# Revit family: Faucet-Lavatory-Grohe-Grandera-23312_Series
name_source: partatom
category: Plumbing Fixtures
revit_build: Autodesk Revit 2014 (Build: 20130308_1515(x64)
units: mm (PartAtom-declared; Revit-internal decimal feet)

## types (4) — shared parameters
ADA Compliant = Yes
Assembly Code = D2020300
CW Connection = Yes
CWFU = 1.5
CalGreen Compliant = Yes
Cold Water Connection Diameter = 3/8"
Default Elevation = 0"
Description = Grandera Single-lever basin mixer 1/2" M-Size
HW Connection = Yes
HWFU = 1.5
Height = 6 7/8"
Hot Water Connection Diameter = 0"
Installation Type = Deck-Mounted
Length = 4 3/8"
Manufacturer = Grohe
Price = Prices may vary. Please consult Manufacturer Representative for most up-to-date price list.
Product Page URL = https://www.grohe.com
URL = http://www.grohe.com
Vent Connection = No
Warranty Documentation Link = https://cdn.cloud.grohe.com
Waste Connection = No
cUPC Compliant = Yes
zero-valued in all types: WFU

## per-type parameters (varying)
| type | Finish | Flow Rate | Material | Shipping Weight |
| 23312000 | Metal-Grohe-000-Chrome | 1.5 gpm (5.7 L/min) | Metal-Grohe-000-Chrome | 4.07 lb |
| 2331200A | Metal-Grohe-00A-Chrome | 1.2 gpm (4.56 L/min) | Metal-Grohe-00A-Chrome | 4.07 lb |
| 23312EN0 | Metal-Grohe-EN0-Brushed Nickel | 1.5 gpm (5.7 L/min) | Metal-Grohe-EN0-Brushed Nickel | 4.00 lb |
| 23312ENA | Metal-Grohe-ENA-Brushed Nickel | 1.2 gpm (4.56 L/min) | Metal-Grohe-ENA-Brushed Nickel | 4.00 lb |

note: column(s) folded — value = type name in every type: Model

## geometry (parser evidence)
native form markers: Sweep x1
no freeform markers — native parametric forms only
